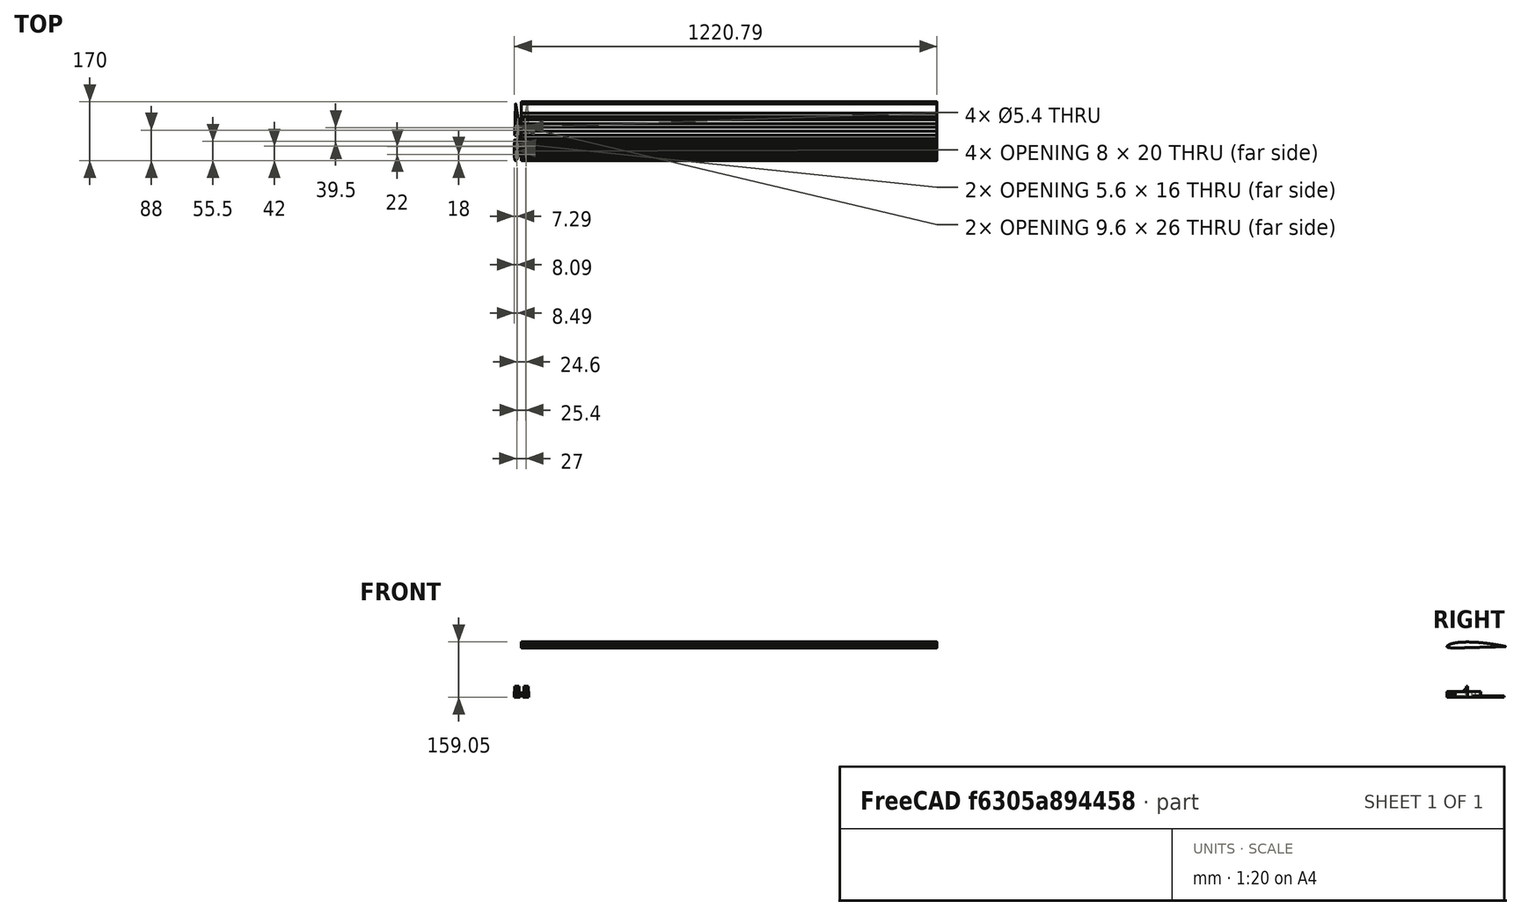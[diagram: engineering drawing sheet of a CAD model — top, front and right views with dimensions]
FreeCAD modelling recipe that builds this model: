
FCSTD DOCUMENT  (FreeCAD 0.18R4 (GitTag))
Label: AirfoilsPrintable_0
License: All rights reserved
LicenseURL: http://en.wikipedia.org/wiki/All_rights_reserved
objects: Part::Cut×2, Part::Part2DObjectPython×2, App::DocumentObjectGroup×1, Part::Extrusion×1
note: 5 computed .brp shape members not serialized (recipe doc carries the construction recipe); baked Part::Feature solids carry a one-line shape summary decoded from their .brp

FEATURE [Part::Cut] Cut071  label="Cut074"
  Placement = pos=(0,0,-10) rot=(0,-1,0;1.5708rad)
FEATURE [Part::Cut] Cut072  label="Cut075"
  Placement = pos=(0,0,0) rot=(0,1,0;1.5708rad)
FEATURE [App::DocumentObjectGroup] ClarkY
FEATURE [Part::Part2DObjectPython] Wire  # Draft 2D object (typed FeaturePython)
  ChamferSize = 0
  Closed = true
  End = (1,0,0)
  FilletRadius = 0
  Length = 2.04451
  MakeFace = true
  Points = (69) [(1,0,0),(0.99572,0.00115,0),(0.98296,0.00448,0),(0.96194,0.00972,0),(0.93301,0.01656,0),(0.89668,0.02475,0),(0.85355,0.034,0),(0.80438,0.04394,0),+61 more]
  Start = (1,0,0)
  Subdivisions = 0
FEATURE [Part::Part2DObjectPython] Clone2D  label="Wire (2D)"  # Draft 2D object (typed FeaturePython)
  Fuse = false
  Objects = -> [Wire]
  Placement = pos=(17,-135,0) rot=(0,0,1;1.5708rad)
  Scale = (170,140,200)
FEATURE [Part::Extrusion] Extrude
  Base = -> Clone2D
  Dir = (0,0,1)
  DirMode = 2
  FaceMakerClass = Part::FaceMakerBullseye
  LengthFwd = 1200
  LengthRev = 0
  Placement = pos=(0,0,0) rot=(0,1,0;1.5708rad)
  Solid = false
  Symmetric = false
